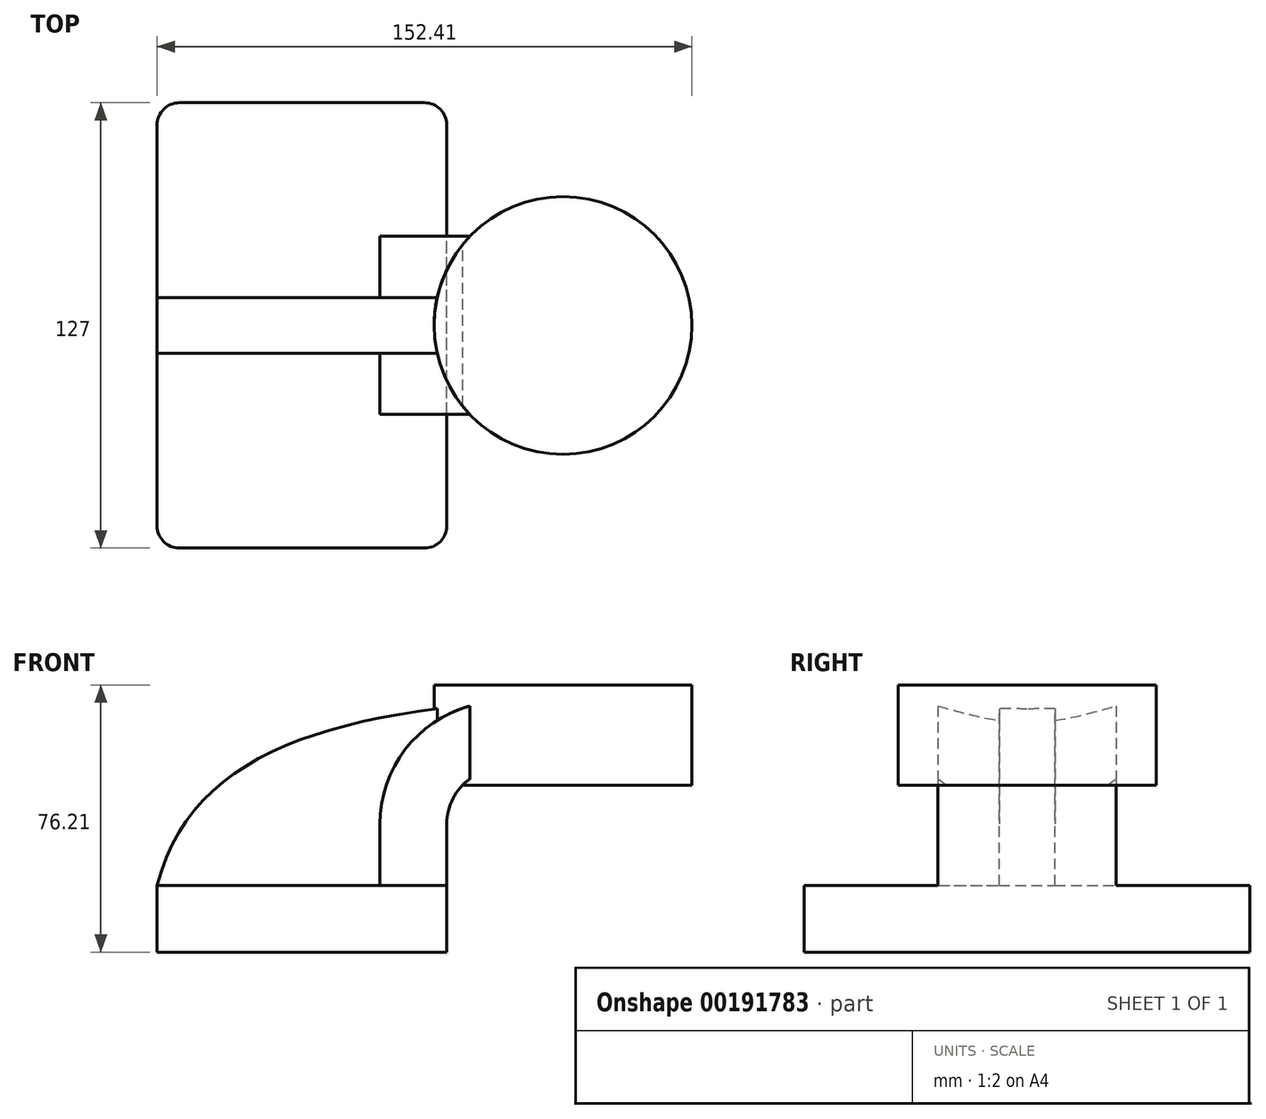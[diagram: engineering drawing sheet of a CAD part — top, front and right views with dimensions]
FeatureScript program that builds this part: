
annotation { "Feature Type Name" : "Feature", "Feature Type Description" : "" }
export const myFeature = defineFeature(function(context is Context, id is Id, definition is map)
    precondition{}
    {
        {
            var Q0;
            Q0=qCreatedBy(makeId("Front.planeOp"),FACE);
            var sketch = newSketch(context, id + "F0", { "sketchPlane" : qUnion([Q0])});
            skLineSegment(sketch, "E0.bottom", {"start": v(-41.28, -9.53) * mm, "end": v(41.28, -9.53) * mm});
            skLineSegment(sketch, "E0.top", {"start": v(-41.28, 9.53) * mm, "end": v(41.28, 9.53) * mm});
            skLineSegment(sketch, "E0.left", {"start": v(-41.28, -9.53) * mm, "end": v(-41.28, 9.53) * mm});
            skLineSegment(sketch, "E0.right", {"start": v(41.28, -9.53) * mm, "end": v(41.28, 9.52) * mm});
            skPoint(sketch, "E0.middle", {"position": v(0, 0) * mm});
            skLineSegment(sketch, "E1.bottom", {"start": v(60.32, 38.1) * mm, "end": v(111.12, 38.1) * mm});
            skLineSegment(sketch, "E1.top", {"start": v(60.32, 66.67) * mm, "end": v(111.12, 66.67) * mm});
            skLineSegment(sketch, "E1.left", {"start": v(60.32, 38.1) * mm, "end": v(60.32, 66.68) * mm});
            skLineSegment(sketch, "E1.right", {"start": v(111.12, 38.1) * mm, "end": v(111.12, 66.68) * mm});
            skPoint(sketch, "E1.middle", {"position": v(85.72, 52.39) * mm});
            skLineSegment(sketch, "E2", {"start": v(41.27, 9.52) * mm, "end": v(41.27, 27) * mm});
            skArc(sketch, "E3", {"start": v(41.28, 27) * mm, "mid": v(45.92, 38.23) * mm, "end": v(57.15, 42.88) * mm});
            skLineSegment(sketch, "E4", {"start": v(57.15, 42.88) * mm, "end": v(74.19, 42.88) * mm});
            skLineSegment(sketch, "E5.0", {"start": v(57.15, 61.93) * mm, "end": v(74.19, 61.93) * mm});
            skArc(sketch, "E5.1", {"start": v(22.23, 27) * mm, "mid": v(32.45, 51.7) * mm, "end": v(57.15, 61.93) * mm});
            skLineSegment(sketch, "E5.2", {"start": v(22.23, 9.52) * mm, "end": v(22.23, 27) * mm});
            skLineSegment(sketch, "E6", {"start": v(74.4, 38.1) * mm, "end": v(74.4, 66.67) * mm});
            skFitSpline(sketch, "E7", {"points": [v(-41.28, 9.53) * mm, v(57.15, 61.93) * mm], "startDerivative": vector(28.04, 109.47) * mm, "endDerivative": vector(157.45, 13.3) * mm});
            skSolve(sketch);
        }
        {
            var Q0;
            Q0=makeQuery(id+"F0.imprint","IMPRINT",FACE,{"disambiguationData":[TD([[makeQuery(id+"F0.imprint","IMPRINT",EDGE,{"derivedFrom":sQuery(id+"F0.wireOp",EDGE,"E0.bottom")}),1.0]])]});
            extrude(context, id + "F1", {"entities" : qUnion([Q0]), "endBound" : BoundingType.SYMMETRIC, "depth" : 127 * mm});
        }
        {
            var Q0;
            {var subQ1=sQuery(id+"F0.wireOp",EDGE,"E2");Q0=makeQuery(id+"F0.imprint","IMPRINT",FACE,{"disambiguationData":[TD([[makeQuery(id+"F0.imprint","IMPRINT",EDGE,{"derivedFrom":subQ1}),1.0]])]});}
            var Q1;
            {var subQ7=sQuery(id+"F0.wireOp",EDGE,"E6");Q1=makeQuery(id+"F0.imprint","IMPRINT",FACE,{"disambiguationData":[TD([[makeQuery(id+"F0.imprint","IMPRINT",EDGE,{"derivedFrom":subQ7}),1.0]])]});}
            extrude(context, id + "F2", {"entities" : qUnion([Q0, Q1]), "operationType" : NewBodyOperationType.ADD, "endBound" : BoundingType.SYMMETRIC, "depth" : 50.8 * mm});
        }
        {
            var Q0;
            {var subQ3=sQuery(id+"F0.wireOp",EDGE,"E5.2");Q0=makeQuery(id+"F0.imprint","IMPRINT",FACE,{"disambiguationData":[TD([[makeQuery(id+"F0.imprint","IMPRINT",EDGE,{"derivedFrom":subQ3}),1.0]])]});}
            extrude(context, id + "F3", {"entities" : qUnion([Q0]), "operationType" : NewBodyOperationType.ADD, "endBound" : BoundingType.SYMMETRIC, "depth" : 15.88 * mm});
        }
        {
            var Q0;
            {var subQ0=sQuery(id+"F0.wireOp",EDGE,"E1.right");Q0=makeQuery(id+"F0.imprint","IMPRINT",FACE,{"disambiguationData":[TD([[makeQuery(id+"F0.imprint","IMPRINT",EDGE,{"derivedFrom":subQ0}),1.0]])]});}
            var Q1;
            Q1=sQuery(id+"F0.wireOp",EDGE,"E6");
            revolve(context, id + "F4", {"operationType" : NewBodyOperationType.ADD, "entities" : qUnion([Q0]), "axis" : qUnion([Q1]), "revolveType" : RevolveType.FULL});
        }
        {
            var Q0;
            Q0=makeQuery(id+"F1.opExtrude","CAP_EDGE",EDGE,{"disambiguationData":[OSD([sQuery(id+"F0.wireOp",EDGE,"E0.left")])],"isStart":false});
            var Q1;
            Q1=makeQuery(id+"F1.opExtrude","CAP_EDGE",EDGE,{"disambiguationData":[OSD([sQuery(id+"F0.wireOp",EDGE,"E0.right")])],"isStart":false});
            var Q2;
            Q2=makeQuery(id+"F1.opExtrude","CAP_EDGE",EDGE,{"disambiguationData":[OSD([sQuery(id+"F0.wireOp",EDGE,"E0.right")])],"isStart":true});
            var Q3;
            Q3=makeQuery(id+"F1.opExtrude","CAP_EDGE",EDGE,{"disambiguationData":[OSD([sQuery(id+"F0.wireOp",EDGE,"E0.left")])],"isStart":true});
            fillet(context, id + "F5", {"entities" : qUnion([Q0, Q1, Q2, Q3]), "radius" : 6.35 * mm, "tangentPropagation" : true, "allowEdgeOverflow" : false});
        }
    });
